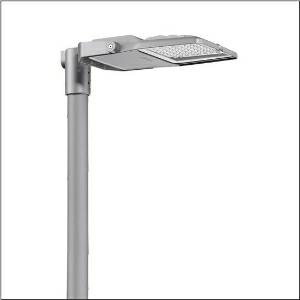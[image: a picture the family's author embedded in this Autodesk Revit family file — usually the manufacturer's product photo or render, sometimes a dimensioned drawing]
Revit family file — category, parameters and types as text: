
# Revit family: floodlight_fl_21_iq_mini___pl43_5xa7771c2a3a_69d2
name_source: partatom
category: Lighting Fixtures
units: mm (PartAtom-declared; Revit-internal decimal feet)

## family parameters
Cut with Voids When Loaded = No
Host = Face
Light Source = No
Part Type = Normal
Room Calculation Point = No
Round Connector Dimension = Use Diameter
Shared = No

## types (1)
- --- (1 x LED, 12520 lm, 87.2 W, 3000K)
    Apparent Load = 87 VA
    CIE Flux Codes = 27 78 99 100 100
    Color Rendering = 70
    Color Temperature = 3000K
    Default Elevation = 1800 mm
    Description = Floodlight FL 21 iQ mini, floodlight, primary light control with lens, of PMMA, primary optical cover: protective disc, of toughened safety glass, transparent, light distribution: PL43, light emission: direct distribution, installation type: surface-mounted, lamps: LED, High Power LED, rated values: 12.520lm | 87,2W | 143,6lm/W (begin service life); end service life: 12.520lm | 92,1W; at 50% lumin. flux: 6.260lm | 40,1W | 156,1lm/W, colour temperature: 3000K, colour rendering: CRI > 70, light colour: 730, light setting 1 begin service life: 100% | 12.520lm | 87,2W | 143,6lm/W | 3.000K, light setting 1 end service life: 92,1W, further light settings possible, control: Auto-Match, Temp-Guard, Lumen-Switch, Night-Set, Smart-Wire, Light-Fading, Desk-Remote (wireless, voltage-free reading and setting of iQ features in the workshop via application-optimized NFC function/RFID function), optimised constant luminous flux control (CLO 2.0), pre-setting: linear dimming characteristic, with terminal, 6-pole, mains connection: 220..240V, AC, 50/60Hz, luminaire housing, of diecast aluminium, powder-coated, SITECO metallic grey (DB 702S), corrosivity category C5 mid according to DIN EN ISO 12944suitable for swimming poolschlorine-resistant, sealing non-destructively replaceable, please order mast flange separately, mast bracket, of steel, galvanised, powder-coated, SITECO metallic grey (DB 702S), protection rating (complete): IP66, insulation class (complete): insulation class II (safety insulation), certification: CE, ENEC, VDE, protection symbol: D, impact resistance: IK08, permissible operating ambient temperature: -40..+40°C, permissible operating ambient temperature for outdoor applications: -40..+50°C, standard: DIN EN 12944, LABS conformity tested according to VDMA 24364:2018-05, packaging unit: 1 piece

Light Distribution: PL43
    Height = 70 mm
    Lamp = 1 x LED
    Lamp Light Flux = 12520 lm
    Lamp Power = 87.2 W
    Lamp count = 1
    Length = 485 mm
    Luminous efficacy = 144 lm/W
    Manufacturer = Siteco
    ModVariant = No
    Model = 5XA7771C2A3A
    Number of Poles = 1
    OnlyDefault = Yes
    Power Factor = 1
    Product Name = Floodlight FL 21 iQ mini | PL43
    Product group = floodlight | pylon annexe
    ProductGroupID = 6201
    Protection Class = Protection class II
    Protection Degree = IP 66
    RLX_Detail_Level = 1
    RLX_Emergency_Light_Flux = 0 lm
    RLX_Emergency_Type = 0
    RLX_Emergency_Type_DB = No
    RlxData = <blob elided: 101377 chars, md5=a25860b4>
    Socket = socket
    Standby Power = 0 W
    System Light Flux = 12520 lm
    System Power = 87 W
    Type Comments = factory setting: luminous flux: 100 % | dim-lin: 254 | 456 mA
    Type Image = l_1007125.jpg
    URL = http://relux.com
    VarID = @adj_161963
    Voltage = 0 V
    Weight = 0.00 kg
    Width = 337 mm

## geometry (parser evidence)
native form markers: Blend x4, Sweep x14
no freeform markers — native parametric forms only
